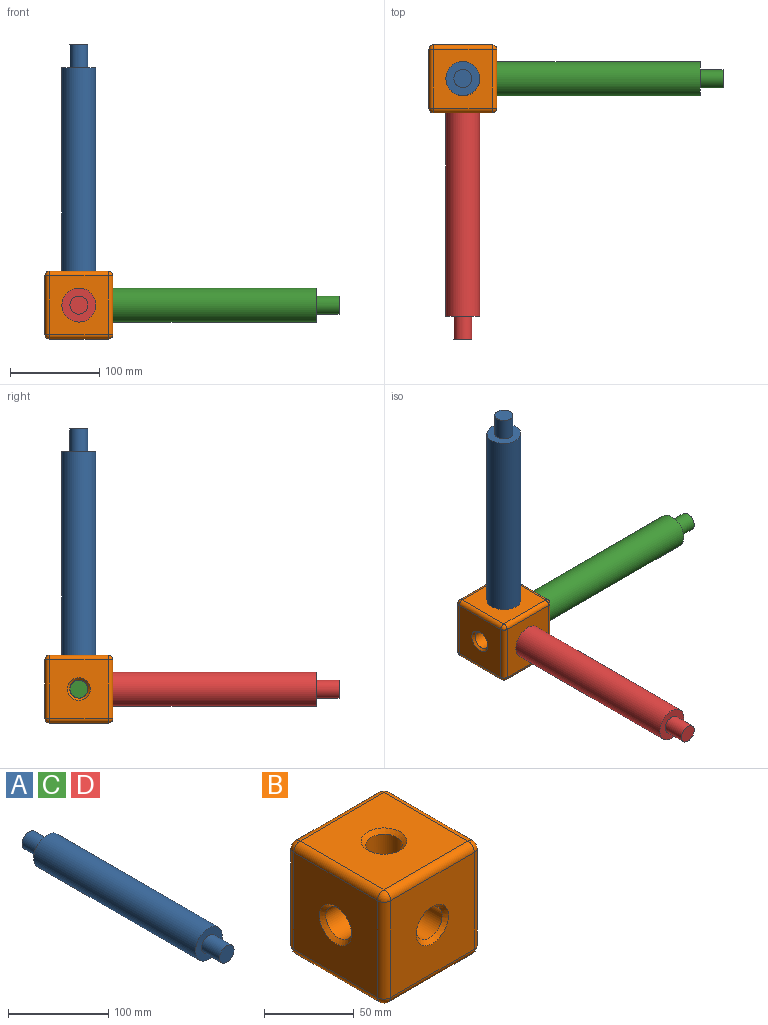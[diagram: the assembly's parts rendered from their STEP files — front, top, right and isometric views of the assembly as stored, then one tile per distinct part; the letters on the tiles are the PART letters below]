
ASSEMBLY  parts=4 mates=7
PART A: 7 faces, bbox 38.1x279.4x38.1 mm
  f0: cylinder r=19.05mm len=228.6mm, axis (0,1,0), area 27362.2mm2, adj f1,f2
  f1: plane 38.1x38.1mm, normal (0,-1,0), area 815.8mm2, adj f0,f3
  f2: plane 38.1x38.1mm, normal (0,1,0), area 815.8mm2, adj f0,f5
  f3: cylinder r=10.16mm len=25.4mm, axis (0,1,0), area 1621.5mm2, adj f1,f4
  f4: plane 20.32x20.32mm, normal (0,-1,0), area 324.3mm2, adj f3
  f5: cylinder r=10.16mm len=25.4mm, axis (0,-1,0), area 1621.5mm2, adj f2,f6
  f6: plane 20.32x20.32mm, normal (0,1,0), area 324.3mm2, adj f5
PART B: 38 faces, bbox 76.2x76.2x76.2 mm
  f0: cylinder r=10.16mm len=28.38mm, axis (-1,0,0), area 1686.1mm2, adj f8,f9,f10,f11,f32
  f1: plane 66.04x66.04mm, normal (-1,0,0), area 3854.6mm2, adj f20,f25,f28,f31,f32
  f2: plane 66.04x66.04mm, normal (0,-1,0), area 3854.6mm2, adj f17,f26,f27,f31,f35
  f3: plane 66.04x66.04mm, normal (1,0,0), area 3854.6mm2, adj f12,f16,f17,f18,f36
  f4: plane 66.04x66.04mm, normal (0,1,0), area 3854.6mm2, adj f12,f15,f19,f20,f34
  f5: plane 66.04x66.04mm, normal (0,0,1), area 3854.6mm2, adj f15,f16,f25,f26,f33
  f6: plane 66.04x66.04mm, normal (0,0,-1), area 3854.6mm2, adj f18,f19,f27,f28,f37
  f7: cylinder r=10.16mm len=28.38mm, axis (-1,0,0), area 1686.1mm2, adj f8,f9,f10,f11,f36
  f8: cylinder r=10.16mm len=28.38mm, axis (0,0,-1), area 1686.1mm2, adj f0,f7,f10,f11,f37
  f9: cylinder r=10.16mm len=28.38mm, axis (0,0,-1), area 1686.1mm2, adj f0,f7,f10,f11,f33
  f10: cylinder r=10.16mm len=28.38mm, axis (0,-1,0), area 1686.1mm2, adj f0,f7,f8,f9,f34
  f11: cylinder r=10.16mm len=28.38mm, axis (0,-1,0), area 1686.1mm2, adj f0,f7,f8,f9,f35
  f12: cylinder r=5.08mm len=66.04mm, axis (0,0,-1), area 527mm2, adj f3,f4,f13,f14
  f13: sphere r=5.08mm, area 40.5mm2, adj f12,f15,f16
  f14: sphere r=5.08mm, area 40.5mm2, adj f12,f18,f19
  f15: cylinder r=5.08mm len=66.04mm, axis (1,0,0), area 527mm2, adj f4,f5,f13,f21
  f16: cylinder r=5.08mm len=66.04mm, axis (0,-1,0), area 527mm2, adj f3,f5,f13,f22
  f17: cylinder r=5.08mm len=66.04mm, axis (0,0,1), area 527mm2, adj f2,f3,f22,f23
  f18: cylinder r=5.08mm len=66.04mm, axis (0,1,0), area 527mm2, adj f3,f6,f14,f23
  f19: cylinder r=5.08mm len=66.04mm, axis (-1,0,0), area 527mm2, adj f4,f6,f14,f24
  f20: cylinder r=5.08mm len=66.04mm, axis (0,0,1), area 527mm2, adj f1,f4,f21,f24
  f21: sphere r=5.08mm, area 40.5mm2, adj f15,f20,f25
  f22: sphere r=5.08mm, area 40.5mm2, adj f16,f17,f26
  f23: sphere r=5.08mm, area 40.5mm2, adj f17,f18,f27
  f24: sphere r=5.08mm, area 40.5mm2, adj f19,f20,f28
  f25: cylinder r=5.08mm len=66.04mm, axis (0,1,0), area 527mm2, adj f1,f5,f21,f29
  f26: cylinder r=5.08mm len=66.04mm, axis (-1,0,0), area 527mm2, adj f2,f5,f22,f29
  f27: cylinder r=5.08mm len=66.04mm, axis (1,0,0), area 527mm2, adj f2,f6,f23,f30
  f28: cylinder r=5.08mm len=66.04mm, axis (0,-1,0), area 527mm2, adj f1,f6,f24,f30
  f29: sphere r=5.08mm, area 40.5mm2, adj f25,f26,f31
  f30: sphere r=5.08mm, area 40.5mm2, adj f27,f28,f31
  f31: cylinder r=5.08mm len=66.04mm, axis (0,0,-1), area 527mm2, adj f1,f2,f29,f30
  f32: cone r=12.7mm half-angle=45deg, axis (-1,0,0), area 258mm2, adj f0,f1
  f33: cone r=10.16mm half-angle=45deg, axis (0,0,1), area 258mm2, adj f5,f9
  f34: cone r=10.16mm half-angle=45deg, axis (0,1,0), area 258mm2, adj f4,f10
  f35: cone r=10.16mm half-angle=45deg, axis (0,-1,0), area 258mm2, adj f2,f11
  f36: cone r=10.16mm half-angle=45deg, axis (1,0,0), area 258mm2, adj f3,f7
  f37: cone r=10.16mm half-angle=45deg, axis (0,0,-1), area 258mm2, adj f6,f8
PART C: same geometry as A
PART D: same geometry as A
PLACE A rot(axis=(-1,0,0),90deg) t=(-39.09,-6.18,176.98)mm
PLACE B t=(-39.09,-6.18,24.58)mm
PLACE C rot(axis=(0,0,1),90deg) t=(113.31,-6.18,24.58)mm
PLACE D t=(-39.09,-158.58,24.58)mm
MATE slider D.f0 <-> B.f10  axis (0,-1,0) through (-39.09,-44.28,24.58)mm
MATE fastened C.f0 <-> B.f36  axis (-1,0,0) through (-0.99,-6.18,24.58)mm
MATE revolute A.f0 <-> B.f8  axis (0,0,1) through (-39.09,-6.18,291.28)mm
MATE fastened C.f0 <-> B.f3  axis (-1,0,0) through (-0.99,-6.18,24.58)mm
MATE slider A.f0 <-> B.f8  axis (0,0,1) through (-39.09,-6.18,62.68)mm
MATE fastened A.f0 <-> B.f5  axis (0,0,-1) through (-39.09,-6.18,62.68)mm
MATE slider C.f0 <-> B.f36  axis (1,0,0) through (227.61,-6.18,24.58)mm
